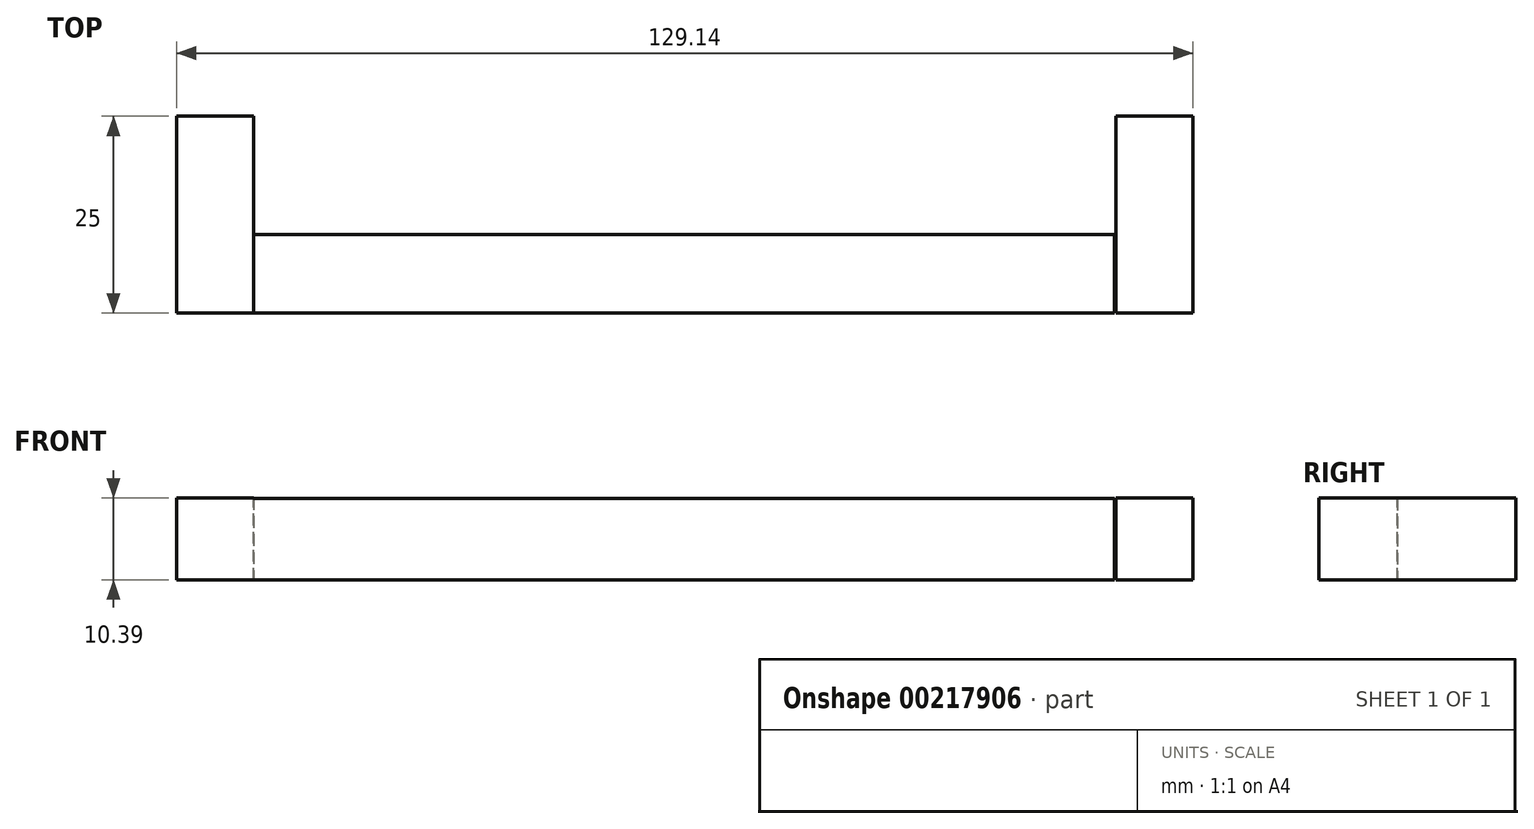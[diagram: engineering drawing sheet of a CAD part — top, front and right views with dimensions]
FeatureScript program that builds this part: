
annotation { "Feature Type Name" : "Feature", "Feature Type Description" : "" }
export const myFeature = defineFeature(function(context is Context, id is Id, definition is map)
    precondition{}
    {
        {
            var Q0;
            Q0=qCreatedBy(makeId("Front.planeOp"),FACE);
            var sketch = newSketch(context, id + "F0", { "sketchPlane" : qUnion([Q0])});
            skLineSegment(sketch, "E0.bottom", {"start": v(-64.57, -25.7) * mm, "end": v(-54.75, -25.7) * mm});
            skLineSegment(sketch, "E0.top", {"start": v(-64.57, -36.08) * mm, "end": v(-54.75, -36.08) * mm});
            skLineSegment(sketch, "E0.left", {"start": v(-64.57, -25.7) * mm, "end": v(-64.57, -36.08) * mm});
            skLineSegment(sketch, "E0.right", {"start": v(-54.75, -25.7) * mm, "end": v(-54.75, -36.08) * mm});
            skLineSegment(sketch, "E1", {"start": v(-64.57, -30.89) * mm, "end": v(-74.68, -30.89) * mm});
            skLineSegment(sketch, "E2", {"start": v(75.24, -30.89) * mm, "end": v(65.41, -30.89) * mm});
            skLineSegment(sketch, "E3.bottom", {"start": v(64.57, -25.7) * mm, "end": v(54.75, -25.7) * mm});
            skLineSegment(sketch, "E3.top", {"start": v(64.57, -36.08) * mm, "end": v(54.75, -36.08) * mm});
            skLineSegment(sketch, "E3.left", {"start": v(64.57, -25.7) * mm, "end": v(64.57, -36.08) * mm});
            skLineSegment(sketch, "E3.right", {"start": v(54.75, -25.7) * mm, "end": v(54.75, -36.08) * mm});
            skSolve(sketch);
        }
        {
            var Q0;
            {var subQ3=sQuery(id+"F0.wireOp",EDGE,"E0.bottom");Q0=makeQuery(id+"F0.imprint","IMPRINT",FACE,{"disambiguationData":[TD([[makeQuery(id+"F0.imprint","IMPRINT",EDGE,{"derivedFrom":subQ3}),-1.0]])]});}
            extrude(context, id + "F1", {"entities" : qUnion([Q0]), "oppositeDirection" : true, "depth" : 25 * mm});
        }
        {
            var Q0;
            Q0=qCreatedBy(makeId("Right.planeOp"),FACE);
            var sketch = newSketch(context, id + "F2", { "sketchPlane" : qUnion([Q0])});
            skLineSegment(sketch, "E4.bottom", {"start": v(0, -25.75) * mm, "end": v(9.94, -25.75) * mm});
            skLineSegment(sketch, "E4.top", {"start": v(0, -36.08) * mm, "end": v(9.94, -36.08) * mm});
            skLineSegment(sketch, "E4.left", {"start": v(0, -25.75) * mm, "end": v(0, -36.08) * mm});
            skLineSegment(sketch, "E4.right", {"start": v(9.94, -25.75) * mm, "end": v(9.94, -36.08) * mm});
            skSolve(sketch);
        }
        {
            var Q0;
            Q0 = qSketchRegion(id + "F2", true);
            extrude(context, id + "F3", {"entities" : qUnion([Q0]), "operationType" : NewBodyOperationType.ADD, "oppositeDirection" : true, "depth" : 55 * mm});
        }
        {
            var Q0;
            Q0=makeQuery(id+"F0.imprint","IMPRINT",FACE,{"disambiguationData":[TD([[makeQuery(id+"F0.imprint","IMPRINT",EDGE,{"derivedFrom":sQuery(id+"F0.wireOp",EDGE,"E3.bottom")}),1.0]])]});
            extrude(context, id + "F4", {"entities" : qUnion([Q0]), "oppositeDirection" : true, "depth" : 25 * mm});
        }
        {
            var Q0;
            Q0 = qSketchRegion(id + "F2", true);
            extrude(context, id + "F5", {"entities" : qUnion([Q0]), "operationType" : NewBodyOperationType.ADD, "depth" : 54.6 * mm});
        }
    });
